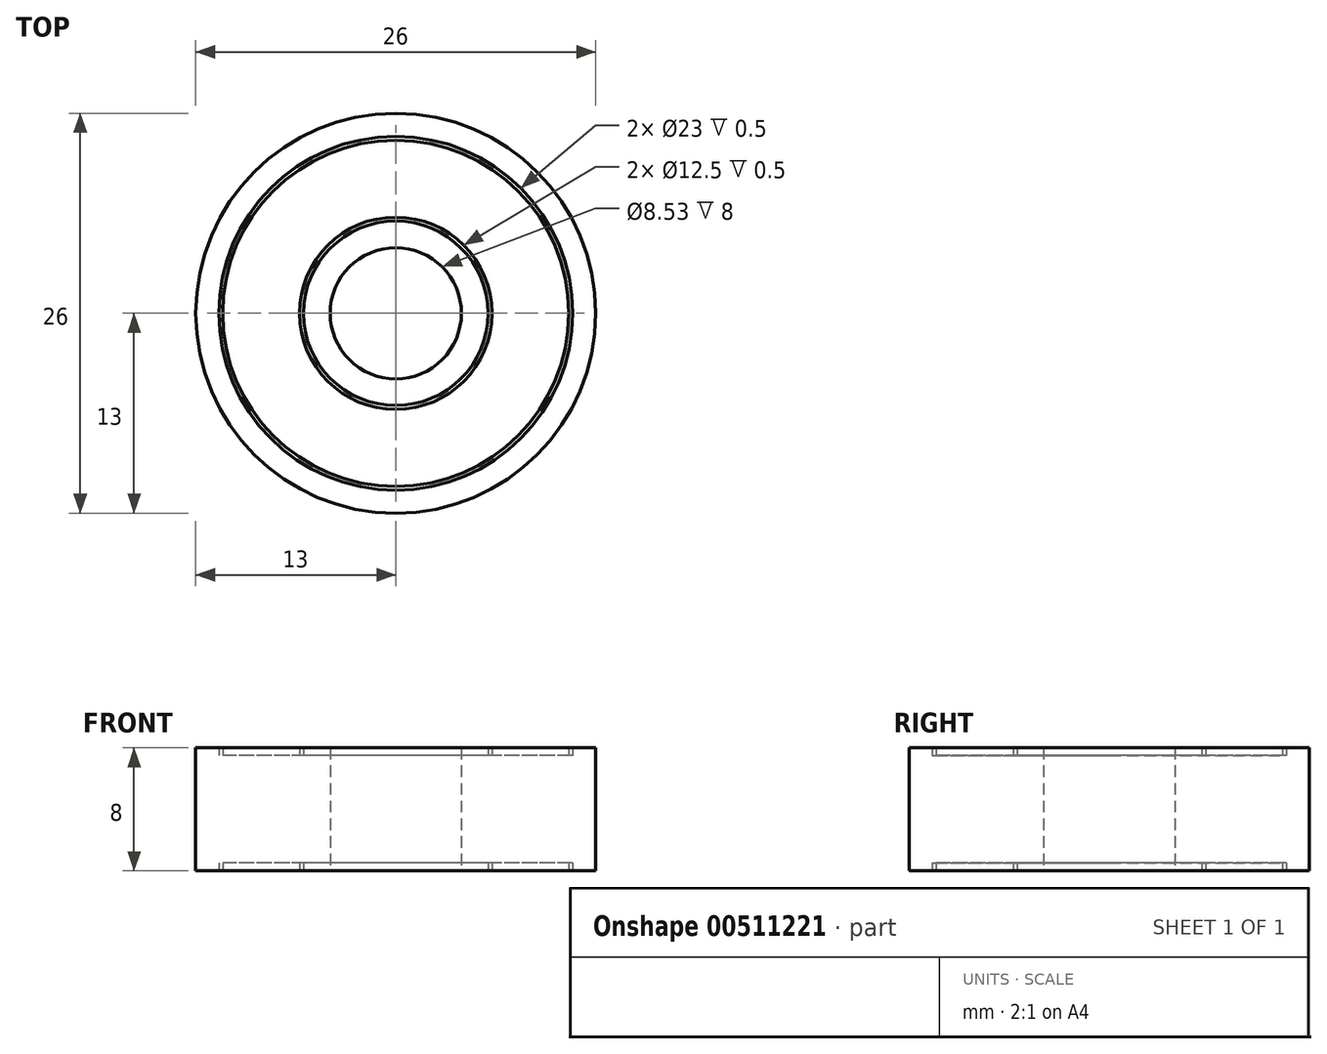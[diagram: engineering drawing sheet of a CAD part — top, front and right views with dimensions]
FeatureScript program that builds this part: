
annotation { "Feature Type Name" : "Feature", "Feature Type Description" : "" }
export const myFeature = defineFeature(function(context is Context, id is Id, definition is map)
    precondition{}
    {
        {
            var Q0;
            Q0=qCreatedBy(makeId("Top.planeOp"),FACE);
            var sketch = newSketch(context, id + "F0", { "sketchPlane" : qUnion([Q0])});
            skCircle(sketch, "E0", {"center": v(0, 0) * mm, "radius": 4.26 * mm});
            skCircle(sketch, "E1", {"center": v(0, 0) * mm, "radius": 13 * mm});
            skCircle(sketch, "E2", {"center": v(0, 0) * mm, "radius": 6 * mm});
            skCircle(sketch, "E3", {"center": v(0, 0) * mm, "radius": 6.25 * mm});
            skCircle(sketch, "E4", {"center": v(0, 0) * mm, "radius": 11.5 * mm});
            skCircle(sketch, "E5", {"center": v(0, 0) * mm, "radius": 11.25 * mm});
            skSolve(sketch);
        }
        {
            var Q0;
            Q0 = qSketchRegion(id + "F0", true);
            var Q1;
            Q1=makeQuery(id+"F0.imprint","IMPRINT",FACE,{"disambiguationData":[TD([[makeQuery(id+"F0.imprint","IMPRINT",EDGE,{"derivedFrom":sQuery(id+"F0.wireOp",EDGE,"E0")}),-1.0]])]});
            var Q2;
            Q2=makeQuery(id+"F0.imprint","IMPRINT",FACE,{"disambiguationData":[TD([[makeQuery(id+"F0.imprint","IMPRINT",EDGE,{"derivedFrom":sQuery(id+"F0.wireOp",EDGE,"E3")}),-1.0]])]});
            extrude(context, id + "F1", {"entities" : qUnion([Q0, Q1, Q2]), "depth" : 8 * mm, "symmetric" : true});
        }
        {
            var Q0;
            Q0=makeQuery(id+"F0.imprint","IMPRINT",FACE,{"disambiguationData":[TD([[makeQuery(id+"F0.imprint","IMPRINT",EDGE,{"derivedFrom":sQuery(id+"F0.wireOp",EDGE,"E2")}),-1.0]])]});
            var Q1;
            Q1=makeQuery(id+"F0.imprint","IMPRINT",FACE,{"disambiguationData":[TD([[makeQuery(id+"F0.imprint","IMPRINT",EDGE,{"derivedFrom":sQuery(id+"F0.wireOp",EDGE,"E4")}),1.0]])]});
            extrude(context, id + "F2", {"entities" : qUnion([Q0, Q1]), "operationType" : NewBodyOperationType.ADD, "depth" : 7 * mm, "symmetric" : true});
        }
    });
